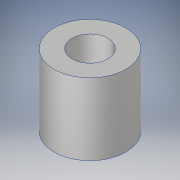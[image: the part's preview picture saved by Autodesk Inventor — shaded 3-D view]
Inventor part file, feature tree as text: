
AUTODESK INVENTOR PART (.ipt)
format: ipt  version: 2017 (Build 210142000, 142)  size: 99,328 bytes
history: native  units: in
note: dims shown in document units (in); Inventor stores cm internally (conversion verified against a paired STEP export)
features: extrude x1, sketch x1
ambient origin geometry x8: Origin, YZ Plane, XZ Plane, XY Plane, X Axis, Y Axis, Z Axis, Center Point
bodies: Solid1 (feature_tree)
feature tree (2):
  extrude  "Extrusion1"  Depth=0.5in
  sketch  "Sketch1"  dims[d0=0.25in d1=0.5in d2=0.5in d3=0.0in]
